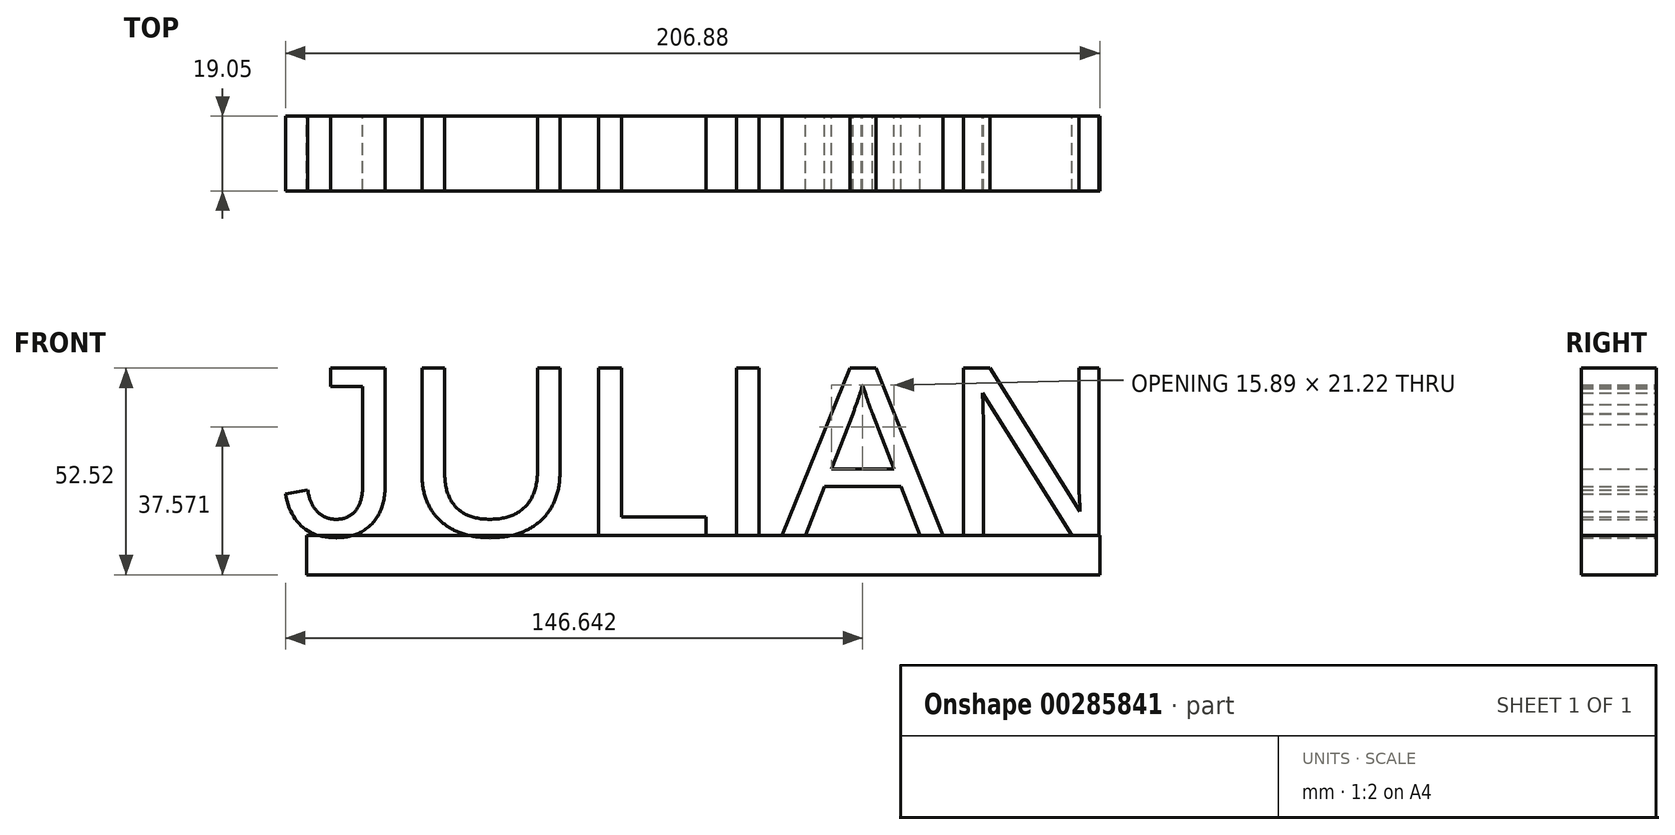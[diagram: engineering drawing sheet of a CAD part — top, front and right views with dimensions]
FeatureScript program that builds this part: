
annotation { "Feature Type Name" : "Feature", "Feature Type Description" : "" }
export const myFeature = defineFeature(function(context is Context, id is Id, definition is map)
    precondition{}
    {
        {
            var Q0;
            Q0=qCreatedBy(makeId("Front.planeOp"),FACE);
            var sketch = newSketch(context, id + "F0", { "sketchPlane" : qUnion([Q0])});
            skText(sketch, "E0", { "text": "JULIAN", "fontName": "Arimo-Regular.ttf"});
            const initialGuessF0  = {"E0": [-0.08272, 0, 1, 0, 0.04445]};
            skSetInitialGuess(sketch, initialGuessF0);
            skSolve(sketch);
        }
        {
            var Q0;
            Q0 = qSketchRegion(id + "F0", true);
            extrude(context, id + "F1", {"entities" : qUnion([Q0]), "depth" : 19.05 * mm});
        }
        {
            var Q0;
            Q0=qCreatedBy(makeId("Front.planeOp"),FACE);
            var sketch = newSketch(context, id + "F2", { "sketchPlane" : qUnion([Q0])});
            skLineSegment(sketch, "E1.bottom", {"start": v(-76.43, 0) * mm, "end": v(125.12, 0) * mm});
            skLineSegment(sketch, "E1.top", {"start": v(-76.43, -10.05) * mm, "end": v(125.12, -10.05) * mm});
            skLineSegment(sketch, "E1.left", {"start": v(-76.43, 0) * mm, "end": v(-76.43, -10.05) * mm});
            skLineSegment(sketch, "E1.right", {"start": v(125.12, 0) * mm, "end": v(125.12, -10.05) * mm});
            skSolve(sketch);
        }
        {
            var Q0;
            Q0 = qSketchRegion(id + "F2", true);
            extrude(context, id + "F3", {"entities" : qUnion([Q0]), "depth" : 19.05 * mm});
        }
    });
